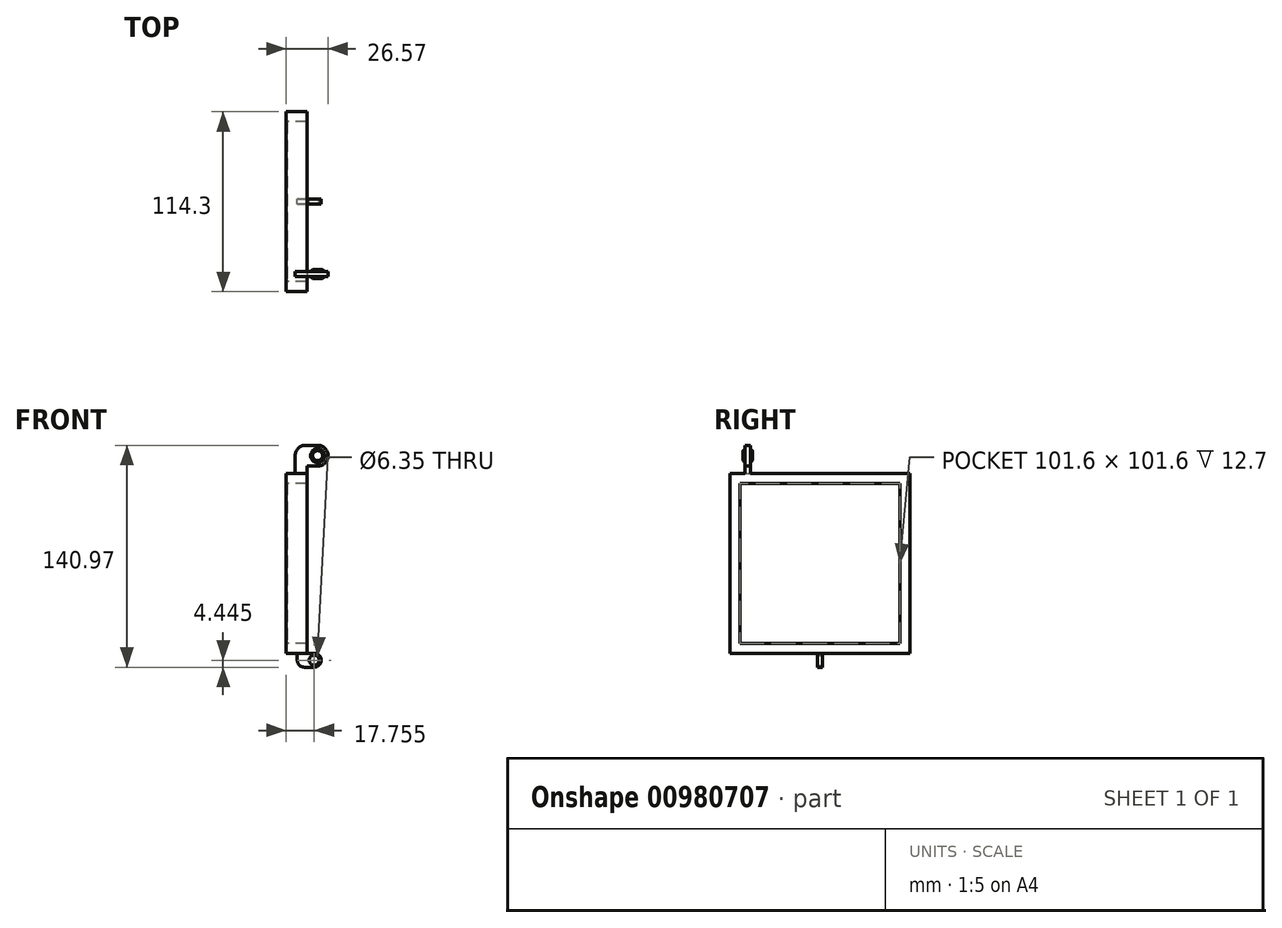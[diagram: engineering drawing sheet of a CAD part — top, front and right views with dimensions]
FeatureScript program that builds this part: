
annotation { "Feature Type Name" : "Feature", "Feature Type Description" : "" }
export const myFeature = defineFeature(function(context is Context, id is Id, definition is map)
    precondition{}
    {
        {
            var Q0;
            Q0=qCreatedBy(makeId("Right.planeOp"),FACE);
            var sketch = newSketch(context, id + "F0", { "sketchPlane" : qUnion([Q0])});
            skLineSegment(sketch, "E0.bottom", {"start": v(57.15, 57.15) * mm, "end": v(-57.15, 57.15) * mm});
            skLineSegment(sketch, "E0.top", {"start": v(57.15, -57.15) * mm, "end": v(-57.15, -57.15) * mm});
            skLineSegment(sketch, "E0.left", {"start": v(57.15, 57.15) * mm, "end": v(57.15, -57.15) * mm});
            skLineSegment(sketch, "E0.right", {"start": v(-57.15, 57.15) * mm, "end": v(-57.15, -57.15) * mm});
            skPoint(sketch, "E0.middle", {"position": v(0, 0) * mm});
            skLineSegment(sketch, "E1.bottom", {"start": v(50.8, 50.8) * mm, "end": v(-50.8, 50.8) * mm});
            skLineSegment(sketch, "E1.top", {"start": v(50.8, -50.8) * mm, "end": v(-50.8, -50.8) * mm});
            skLineSegment(sketch, "E1.left", {"start": v(50.8, 50.8) * mm, "end": v(50.8, -50.8) * mm});
            skLineSegment(sketch, "E1.right", {"start": v(-50.8, 50.8) * mm, "end": v(-50.8, -50.8) * mm});
            skSolve(sketch);
        }
        {
            var Q0;
            Q0=makeQuery(id+"F0.imprint","IMPRINT",FACE,{"disambiguationData":[TD([[makeQuery(id+"F0.imprint","IMPRINT",EDGE,{"derivedFrom":sQuery(id+"F0.wireOp",EDGE,"E0.bottom")}),1.0]])]});
            extrude(context, id + "F1", {"entities" : qUnion([Q0]), "depth" : 12.7 * mm, "offsetDistance" : 25.4 * mm});
        }
        {
            var Q0;
            Q0=qCreatedBy(makeId("Right.planeOp"),FACE);
            var sketch = newSketch(context, id + "F2", { "sketchPlane" : qUnion([Q0])});
            skLineSegment(sketch, "E2.bottom", {"start": v(-57.15, 57.15) * mm, "end": v(57.15, 57.15) * mm});
            skLineSegment(sketch, "E2.top", {"start": v(-57.15, -57.15) * mm, "end": v(57.15, -57.15) * mm});
            skLineSegment(sketch, "E2.left", {"start": v(-57.15, 57.15) * mm, "end": v(-57.15, -57.15) * mm});
            skLineSegment(sketch, "E2.right", {"start": v(57.15, 57.15) * mm, "end": v(57.15, -57.15) * mm});
            skSolve(sketch);
        }
        {
            var Q0;
            Q0=qSketchRegion(id+"F2",true);
            extrude(context, id + "F3", {"entities" : qUnion([Q0]), "operationType" : NewBodyOperationType.ADD, "oppositeDirection" : true, "depth" : 0.6 * mm, "offsetDistance" : 25.4 * mm});
        }
        {
            var Q0;
            Q0=makeQuery(id+"F3.boolean.opBoolean","MERGE",FACE,{"derivedFrom":[makeQuery(id+"F1.opExtrude","SWEPT_FACE",FACE,{"disambiguationData":[OSD([sQuery(id+"F0.wireOp",EDGE,"E0.bottom")])]}),makeQuery(id+"F3.opExtrude","SWEPT_FACE",FACE,{"disambiguationData":[OSD([sQuery(id+"F2.wireOp",EDGE,"E2.bottom")])]})]});
            var sketch = newSketch(context, id + "F4", { "sketchPlane" : qUnion([Q0])});
            skLineSegment(sketch, "E3.bottom", {"start": v(5.08, -47.63) * mm, "end": v(25.96, -47.63) * mm});
            skLineSegment(sketch, "E3.top", {"start": v(5.08, -44.32) * mm, "end": v(25.96, -44.32) * mm});
            skLineSegment(sketch, "E3.left", {"start": v(5.08, -47.63) * mm, "end": v(5.08, -44.32) * mm});
            skLineSegment(sketch, "E3.right", {"start": v(25.96, -47.63) * mm, "end": v(25.96, -44.32) * mm});
            skSolve(sketch);
        }
        {
            var Q0;
            Q0=qSketchRegion(id+"F4",true);
            extrude(context, id + "F5", {"entities" : qUnion([Q0]), "operationType" : NewBodyOperationType.ADD, "depth" : 17.78 * mm, "offsetDistance" : 25.4 * mm});
        }
        {
            var Q0;
            Q0=makeQuery(id+"F5.opExtrude","CAP_EDGE",EDGE,{"disambiguationData":[OSD([sQuery(id+"F4.wireOp",EDGE,"E3.right")])],"isStart":false});
            fillet(context, id + "F6", {"entities" : qUnion([Q0]), "radius" : 6.63 * mm, "tangentPropagation" : true, "allowEdgeOverflow" : false});
        }
        {
            var Q0;
            Q0=makeQuery(id+"F5.opExtrude","SWEPT_FACE",FACE,{"disambiguationData":[OSD([sQuery(id+"F4.wireOp",EDGE,"E3.bottom")])]});
            var sketch = newSketch(context, id + "F7", { "sketchPlane" : qUnion([Q0])});
            skArc(sketch, "E4", {"start": v(19.33, 61.67) * mm, "mid": v(25.96, 68.3) * mm, "end": v(19.33, 74.93) * mm});
            skLineSegment(sketch, "E5", {"start": v(19.33, 61.67) * mm, "end": v(12.7, 61.67) * mm});
            skLineSegment(sketch, "E6", {"start": v(12.7, 61.67) * mm, "end": v(12.7, 57.15) * mm});
            skLineSegment(sketch, "E7", {"start": v(12.7, 57.15) * mm, "end": v(28.7, 51.03) * mm});
            skLineSegment(sketch, "E8", {"start": v(28.7, 51.03) * mm, "end": v(31.02, 81.44) * mm});
            skLineSegment(sketch, "E9", {"start": v(31.02, 81.44) * mm, "end": v(19.33, 74.93) * mm});
            skSolve(sketch);
        }
        {
            var Q0;
            Q0=qSketchRegion(id+"F7",true);
            extrude(context, id + "F8", {"entities" : qUnion([Q0]), "operationType" : NewBodyOperationType.REMOVE, "oppositeDirection" : true, "depth" : 6.35 * mm, "offsetDistance" : 25.4 * mm});
        }
        {
            var Q0;
            Q0=makeQuery(id+"F5.opExtrude","CAP_EDGE",EDGE,{"disambiguationData":[OSD([sQuery(id+"F4.wireOp",EDGE,"E3.left")])],"isStart":false});
            fillet(context, id + "F9", {"entities" : qUnion([Q0]), "radius" : 6.63 * mm, "tangentPropagation" : true, "allowEdgeOverflow" : false});
        }
        {
            var Q0;
            Q0=makeQuery(id+"F5.opExtrude","SWEPT_FACE",FACE,{"disambiguationData":[OSD([sQuery(id+"F4.wireOp",EDGE,"E3.bottom")])]});
            var sketch = newSketch(context, id + "F10", { "sketchPlane" : qUnion([Q0])});
            skCircle(sketch, "E10", {"center": v(19.33, 68.3) * mm, "radius": 4.45 * mm});
            skSolve(sketch);
        }
        {
            var Q0;
            Q0=qSketchRegion(id+"F10",true);
            extrude(context, id + "F11", {"entities" : qUnion([Q0]), "operationType" : NewBodyOperationType.ADD, "depth" : 1.27 * mm, "offsetDistance" : 25.4 * mm});
        }
        {
            var Q0;
            Q0=makeQuery(id+"F5.opExtrude","SWEPT_FACE",FACE,{"disambiguationData":[OSD([sQuery(id+"F4.wireOp",EDGE,"E3.top")])]});
            var sketch = newSketch(context, id + "F12", { "sketchPlane" : qUnion([Q0])});
            skCircle(sketch, "E11", {"center": v(-19.33, 68.3) * mm, "radius": 4.45 * mm});
            skSolve(sketch);
        }
        {
            var Q0;
            Q0=qSketchRegion(id+"F12",true);
            extrude(context, id + "F13", {"entities" : qUnion([Q0]), "operationType" : NewBodyOperationType.ADD, "depth" : 1.27 * mm, "offsetDistance" : 25.4 * mm});
        }
        {
            var Q0;
            Q0=makeQuery(id+"F11.opExtrude","CAP_EDGE",EDGE,{"disambiguationData":[OSD([sQuery(id+"F10.wireOp",EDGE,"E10")])],"isStart":false});
            var Q1;
            Q1=makeQuery(id+"F13.opExtrude","CAP_EDGE",EDGE,{"disambiguationData":[OSD([sQuery(id+"F12.wireOp",EDGE,"E11")])],"isStart":false});
            chamfer(context, id + "F14", {"entities" : qUnion([Q0, Q1]), "width" : 1.27 * mm, "tangentPropagation" : true});
        }
        {
            var Q0;
            Q0=qCreatedBy(makeId("Front.planeOp"),FACE);
            var sketch = newSketch(context, id + "F15", { "sketchPlane" : qUnion([Q0])});
            skLineSegment(sketch, "E12", {"start": v(6.35, -57.15) * mm, "end": v(6.35, -66.04) * mm});
            skLineSegment(sketch, "E13", {"start": v(6.35, -66.04) * mm, "end": v(21.59, -66.04) * mm});
            skLineSegment(sketch, "E14", {"start": v(21.59, -66.04) * mm, "end": v(21.59, -57.15) * mm});
            skLineSegment(sketch, "E15", {"start": v(21.59, -57.15) * mm, "end": v(6.35, -57.15) * mm});
            skSolve(sketch);
        }
        {
            var Q0;
            Q0=qSketchRegion(id+"F15",true);
            extrude(context, id + "F16", {"entities" : qUnion([Q0]), "operationType" : NewBodyOperationType.ADD, "endBound" : BoundingType.SYMMETRIC, "depth" : 3.17 * mm, "offsetDistance" : 25.4 * mm});
        }
        {
            var Q0;
            Q0=makeQuery(id+"F16.opExtrude","SWEPT_EDGE",EDGE,{"disambiguationData":[OSD([sQuery(id+"F15.wireOp",EDGE,"E14"),sQuery(id+"F15.wireOp",EDGE,"E15")])]});
            var Q1;
            Q1=makeQuery(id+"F16.opExtrude","SWEPT_EDGE",EDGE,{"disambiguationData":[OSD([sQuery(id+"F15.wireOp",EDGE,"E13"),sQuery(id+"F15.wireOp",EDGE,"E14")])]});
            var Q2;
            Q2=makeQuery(id+"F16.opExtrude","SWEPT_EDGE",EDGE,{"disambiguationData":[OSD([sQuery(id+"F15.wireOp",EDGE,"E12"),sQuery(id+"F15.wireOp",EDGE,"E13")])]});
            fillet(context, id + "F17", {"entities" : qUnion([Q0, Q1, Q2]), "radius" : 4.44 * mm, "tangentPropagation" : true, "allowEdgeOverflow" : false});
        }
        {
            var Q0;
            Q0=makeQuery(id+"F16.opExtrude","CAP_FACE",FACE,{"disambiguationData":[OSD([sQuery(id+"F15.wireOp",EDGE,"E12"),sQuery(id+"F15.wireOp",EDGE,"E13"),sQuery(id+"F15.wireOp",EDGE,"E14"),sQuery(id+"F15.wireOp",EDGE,"E15")])],"isStart":true});
            var sketch = newSketch(context, id + "F18", { "sketchPlane" : qUnion([Q0])});
            skCircle(sketch, "E16", {"center": v(-17.14, -61.6) * mm, "radius": 3.18 * mm});
            skSolve(sketch);
        }
        {
            var Q0;
            Q0=qSketchRegion(id+"F18",true);
            extrude(context, id + "F19", {"entities" : qUnion([Q0]), "operationType" : NewBodyOperationType.REMOVE, "oppositeDirection" : true, "depth" : 25.4 * mm, "offsetDistance" : 25.4 * mm});
        }
    });
